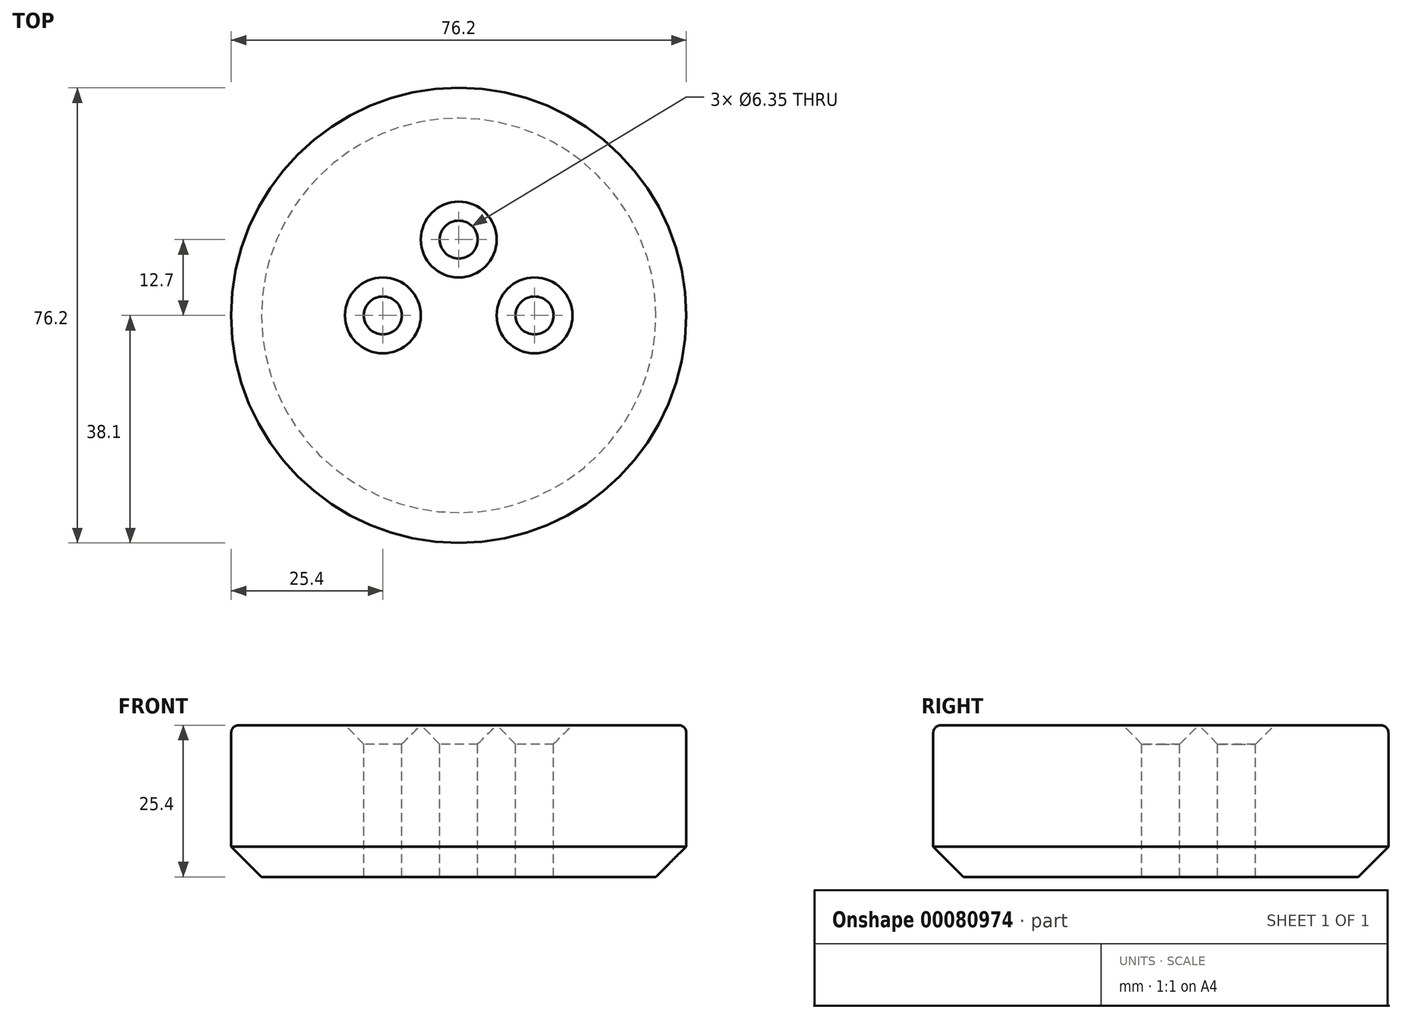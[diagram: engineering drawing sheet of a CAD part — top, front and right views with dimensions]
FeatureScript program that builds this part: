
annotation { "Feature Type Name" : "Feature", "Feature Type Description" : "" }
export const myFeature = defineFeature(function(context is Context, id is Id, definition is map)
    precondition{}
    {
        {
            var Q0;
            Q0=qCreatedBy(makeId("Top.planeOp"),FACE);
            var sketch = newSketch(context, id + "F0", { "sketchPlane" : qUnion([Q0])});
            skCircle(sketch, "E0", {"center": v(0, 0) * mm, "radius": 38.1 * mm});
            skCircle(sketch, "E1", {"center": v(-41.64, 39.14) * mm, "radius": 19.05 * mm});
            skSolve(sketch);
        }
        {
            var Q0;
            Q0=makeQuery(id+"F0.imprint","IMPRINT",FACE,{"disambiguationData":[TD([[makeQuery(id+"F0.imprint","IMPRINT",EDGE,{"derivedFrom":sQuery(id+"F0.wireOp",EDGE,"E0")}),1.0]])]});
            extrude(context, id + "F1", {"entities" : qUnion([Q0]), "depth" : 25.4 * mm});
        }
        {
            var Q0;
            Q0=makeQuery(id+"F1.opExtrude","CAP_FACE",FACE,{"disambiguationData":[OSD([sQuery(id+"F0.wireOp",EDGE,"E0")])],"isStart":false});
            var sketch = newSketch(context, id + "F2", { "sketchPlane" : qUnion([Q0])});
            skPoint(sketch, "E2", {"position": v(-12.7, 0) * mm});
            skPoint(sketch, "E3", {"position": v(12.7, 0) * mm});
            skPoint(sketch, "E4", {"position": v(0, 12.7) * mm});
            skSolve(sketch);
        }
        {
            var Q0;
            Q0=sQuery(id+"F2.wireOp",VERTEX,"E2");
            var Q1;
            Q1=sQuery(id+"F2.wireOp",VERTEX,"E4");
            var Q2;
            Q2=sQuery(id+"F2.wireOp",VERTEX,"E3");
            var Q3;
            Q3=makeQuery(id+"F1.opExtrude","SWEPT_BODY",BODY,{"disambiguationData":[OSD([sQuery(id+"F0.wireOp",EDGE,"E0")])]});
            hole(context, id + "F3", {"style" : HoleStyle.C_SINK, "endStyle" : HoleEndStyle.THROUGH, "holeDiameter" : 6.35 * mm, "cSinkDiameter" : 12.7 * mm, "cSinkAngle" : 90 * degree, "locations" : qUnion([Q0, Q1, Q2]), "scope" : qUnion([Q3]), "isTappedThrough" : true});
        }
        {
            var Q0;
            Q0=makeQuery(id+"F1.opExtrude","CAP_EDGE",EDGE,{"disambiguationData":[OSD([sQuery(id+"F0.wireOp",EDGE,"E0")])],"isStart":false});
            fillet(context, id + "F4", {"entities" : qUnion([Q0]), "radius" : 1.27 * mm, "tangentPropagation" : true, "allowEdgeOverflow" : false});
        }
        {
            var Q0;
            Q0=makeQuery(id+"F1.opExtrude","CAP_EDGE",EDGE,{"disambiguationData":[OSD([sQuery(id+"F0.wireOp",EDGE,"E0")])],"isStart":true});
            chamfer(context, id + "F5", {"entities" : qUnion([Q0]), "width" : 5.08 * mm, "tangentPropagation" : true});
        }
    });
